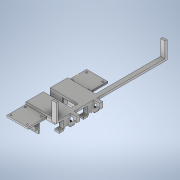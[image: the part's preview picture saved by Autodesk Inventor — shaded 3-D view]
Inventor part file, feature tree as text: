
AUTODESK INVENTOR PART (.ipt)
format: ipt  version: 2020.2 (Build 242310000, 310)  size: 921,088 bytes
history: native  units: mm
features: sketch x35, extrude x35, projected_geometry x17, hole x3
ambient origin geometry x8: Origin, YZ Plane, XZ Plane, XY Plane, X Axis, Y Axis, Z Axis, Center Point
bodies: Solid1 (feature_tree)
feature tree (90):
  sketch  "Sketch1"  dims[d0=8.0mm d1=98.298mm]
  extrude  "Extrusion1"  Depth=98.298mm
  extrude  "Extrusion2"  Depth=4.0mm
  extrude  "Extrusion3"  Depth=4.0mm TaperAngle=0.0deg
  extrude  "Extrusion4"  Depth=34.0mm
  extrude  "Extrusion5"  Depth=12.7mm
  extrude  "Extrusion6"  Depth=25.0mm
  hole  "Hole1"  [1 undecoded]
  extrude  "Extrusion11"  TaperAngle=60.0deg  [1 undecoded]
  extrude  "Extrusion12"  TaperAngle=120.0deg  [1 undecoded]
  sketch  "Sketch16"  dims[d19=6.4262mm d20=120.0deg]
  extrude  "Extrusion13"  Depth=6.4262mm
  extrude  "Extrusion14"  Depth=6.4262mm
  sketch  "Sketch17"  dims[d21=120.0deg d22=6.4262mm]
  extrude  "Extrusion15"  Depth=25.4mm TaperAngle=0.0deg
  extrude  "Extrusion18"  Depth=12.8016mm
  extrude  "Extrusion19"  Depth=12.8016mm
  extrude  "Extrusion20"  Depth=10.0mm
  hole  "Hole2"  [1 undecoded]
  extrude  "Extrusion21"  Depth=2.0mm
  extrude  "Extrusion22"  Depth=2.0mm
  sketch  "Sketch27"  dims[d45=12.8016mm d46=2.0mm]
  extrude  "Extrusion23"  Depth=25.4mm
  extrude  "Extrusion24"  Depth=32.48mm
  extrude  "Extrusion25"  TaperAngle=90.0deg  [1 undecoded]
  sketch  "Sketch29"  dims[d79=51.53mm d80=32.48mm]
  extrude  "Extrusion26"  Depth=2.0mm
  extrude  "Extrusion27"  Depth=21.0mm
  extrude  "Extrusion28"  Depth=36.0mm TaperAngle=0.0deg
  extrude  "Extrusion29"  Depth=8.0mm
  extrude  "Extrusion30"  Depth=17.5mm
  extrude  "Extrusion32"  Depth=35.0mm
  extrude  "Extrusion38"  Depth=5.0mm
  extrude  "Extrusion39"  TaperAngle=90.0deg  [1 undecoded]
  extrude  "Extrusion40"  Depth=5.0mm
  hole  "Hole4"  [1 undecoded]
  extrude  "Extrusion43"  Depth=1.5mm
  extrude  "Extrusion44"  TaperAngle=0.0deg  [1 undecoded]
  extrude  "Extrusion45"  Depth=28.8036mm
  extrude  "Extrusion46"  Depth=12.7mm
  extrude  "Extrusion47"  Depth=12.7mm
  extrude  "Extrusion48"  TaperAngle=120.0deg  [1 undecoded]
  extrude  "Extrusion49"  Depth=12.7mm
  sketch  "Sketch2"  dims[d2=8.0mm d3=4.0mm]
  sketch  "Sketch3"  dims[d4=4.0mm d5=4.0mm d6=0.0mm]
  sketch  "Sketch4"  dims[d7=34.0mm d8=0.0mm d9=19.558mm]
  sketch  "Sketch5"  dims[d10=16.1125mm d11=12.7mm]
  sketch  "Sketch6"  dims[d12=25.0mm d13=0.0mm d14=7.2009mm]
  sketch  "Sketch14"  dims[d15=6.4135mm d16=12.827mm]
  projected_geometry  "Projected Loop2"
  sketch  "Sketch15"  dims[d17=6.4262mm d18=60.0deg]
  projected_geometry  "Projected Loop3"
  sketch  "Sketch18"  dims[d23=120.0deg d24=6.4262mm]
  sketch  "Sketch21"  dims[d25=120.0deg d26=25.4mm d27=0.0mm]
  sketch  "Sketch22"  dims[d28=6.0mm d29=12.8016mm]
  sketch  "Sketch23"  dims[d30=5.9944mm d31=12.8016mm]
  sketch  "Sketch24"  dims[d32=25.4mm d33=0.0mm d34=10.0mm]
  sketch  "Sketch25"  dims[d35=90.0deg d36=20.0mm]
  projected_geometry  "Projected Loop5"
  sketch  "Sketch26"  dims[d37=3.4mm d38=19.05mm d39=6.2992mm d40=6.35mm d41=90.0deg d42=5.0mm d43=0.0mm d44=2.0mm]
  sketch  "Sketch28"  dims[d47=25.4mm d48=0.0mm d78=16.24mm]
  sketch  "Sketch30"  dims[d81=90.0deg d82=90.0deg]
  sketch  "Sketch32"  dims[d83=4.0mm d84=0.0mm d87=2.0mm]
  projected_geometry  "Projected Loop6"
  sketch  "Sketch33"  dims[d88=2.0mm d89=21.0mm]
  projected_geometry  "Projected Loop7"
  sketch  "Sketch35"  dims[d90=2.0mm d91=36.0mm d92=0.0mm]
  projected_geometry  "Projected Loop8"
  sketch  "Sketch42"  dims[d93=17.78mm d94=8.0mm]
  sketch  "Sketch43"  dims[d95=180.0deg d96=17.5mm]
  projected_geometry  "Projected Loop9"
  projected_geometry  "Projected Loop10"
  projected_geometry  "Projected Loop11"
  projected_geometry  "Projected Loop12"
  sketch  "Sketch44"  dims[d97=90.0deg d98=35.0mm]
  sketch  "Sketch45"  dims[d99=3.5mm d100=5.0mm]
  sketch  "Sketch48"  dims[d101=7.0mm d102=90.0deg]
  sketch  "Sketch49"  dims[d103=5.0mm d104=3.4mm]
  projected_geometry  "Projected Loop13"
  projected_geometry  "Projected Loop14"
  sketch  "Sketch50"  dims[d105=3.4mm d106=25.4mm d107=0.0mm]
  projected_geometry  "Projected Loop15"
  sketch  "Sketch51"  dims[d108=6.4262mm d109=0.0mm d110=1.5mm]
  sketch  "Sketch52"  dims[d111=1.5mm d112=0.0mm d113=0.0mm]
  sketch  "Sketch53"  dims[d128=44.8mm d129=28.8036mm]
  projected_geometry  "Projected Loop16"
  projected_geometry  "Projected Loop17"
  projected_geometry  "Projected Loop18"
  projected_geometry  "Projected Loop19"
  sketch  "Sketch54"  dims[d130=25.4mm d131=0.0mm d132=3.2131mm d133=6.4262mm d134=120.0deg d135=3.2131mm d136=6.4262mm d137=120.0deg d138=25.4mm d139=0.0mm d140=8.001mm d141=17.78mm d142=8.001mm d143=0.0mm d144=25.4mm d145=0.0mm d146=10.0mm d147=20.0mm d148=3.4mm d149=19.05mm d150=6.2992mm d151=6.35mm d152=90.0deg d153=5.0mm d154=0.0mm d155=16.2433mm d156=32.4866mm d157=51.5366mm d158=4.0mm d159=0.0mm d160=21.0mm d161=2.0mm d162=2.0mm d163=2.0mm d164=2.0mm d165=36.0mm d166=0.0mm d167=7.0mm d168=5.0mm d169=5.0mm d170=17.5mm d171=35.0mm d172=3.4mm d173=3.4mm d174=5.0mm d175=0.0mm d176=5.0mm d177=0.0mm d178=1.5mm d179=1.5mm d180=25.4mm d181=0.0mm d182=19.05mm d183=10.0mm d184=5.08mm d185=4.0mm d186=0.0mm d187=10.0mm d188=0.0mm d189=2.0mm d190=3.0mm d191=25.4mm d192=0.0mm d194=30.0mm d195=0.0mm d196=102.489mm d197=0.0mm d201=11.43mm d202=0.0mm d239=25.4mm d240=0.0mm d241=1.5mm d242=0.0mm d243=39.0mm d244=35.0mm d245=39.0mm d246=35.0mm d247=3.0mm d248=0.0mm d249=5.0mm d250=5.0mm d251=29.7mm d252=26.05mm d253=4.0mm d254=4.0mm d255=29.7mm d256=26.05mm d257=3.4mm d258=19.05mm d259=6.2992mm d260=6.35mm d261=90.0deg d262=25.4mm d263=20.594885mm d271=4.0mm d272=28.4mm d273=0.0mm d274=25.4mm d275=0.0mm d276=3.429mm d277=180.0deg d278=30.0mm d279=0.0mm d280=6.35mm d281=25.4mm d282=0.0mm d283=5.08mm d284=25.4mm d285=0.0mm d286=2.0mm d287=0.0mm d288=12.7mm d289=0.0mm d214=12.7mm d215=0.872665mm d216=12.7mm d217=0.872665mm d228=12.7mm d229=0.872665mm d230=12.7mm d231=0.872665mm]
note: 9 required parameter values undecoded (feature->parameter linkage not recoverable at this tier; creation-order binding heuristic only, values carry confidence <= 0.55)
